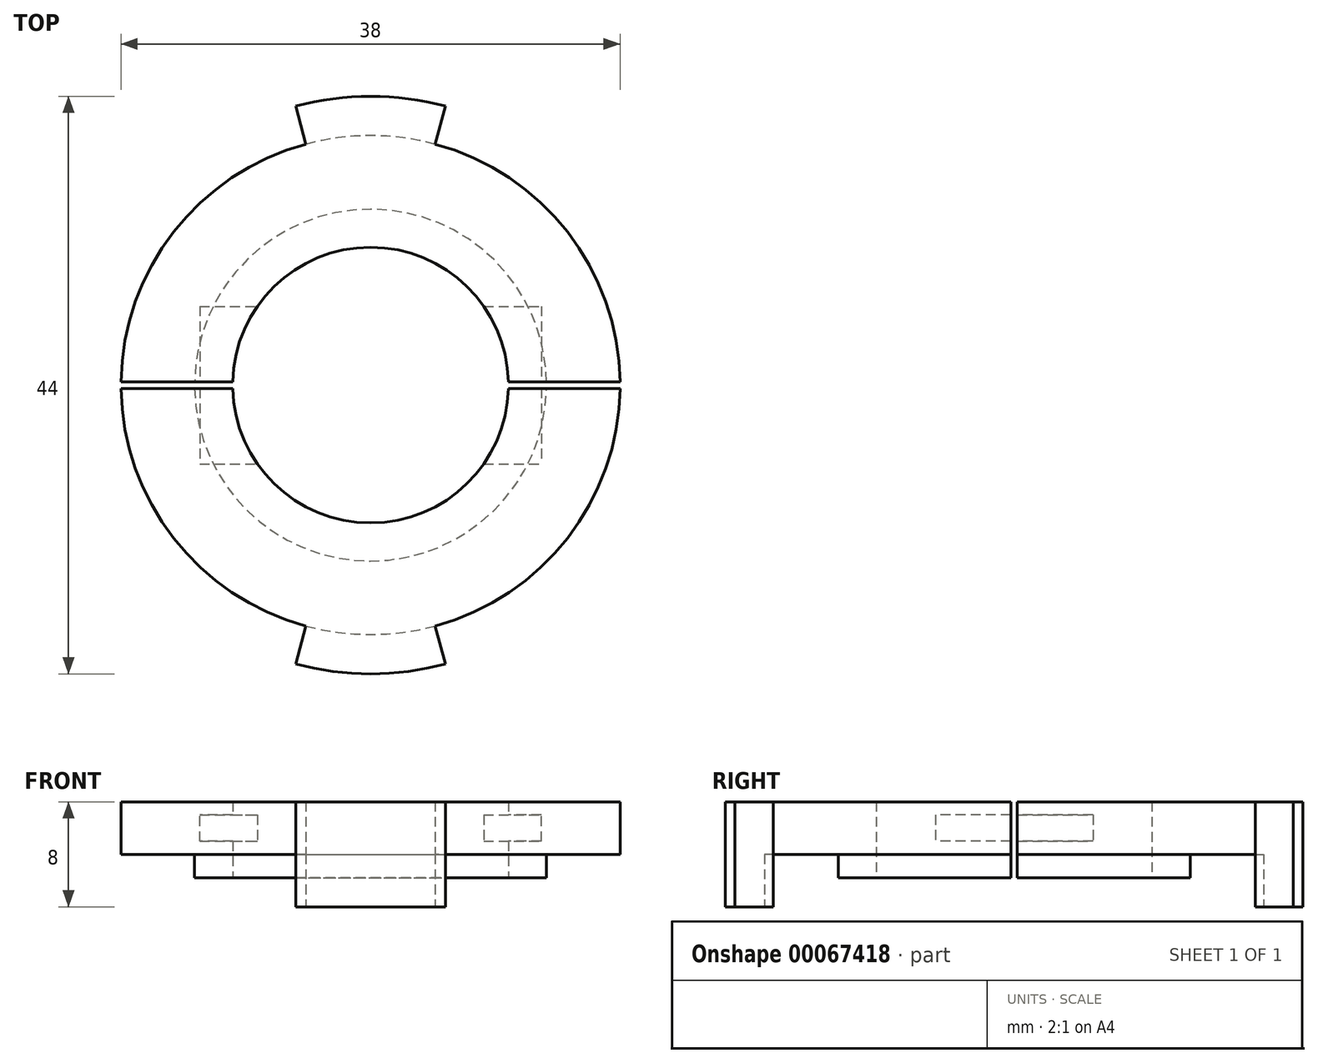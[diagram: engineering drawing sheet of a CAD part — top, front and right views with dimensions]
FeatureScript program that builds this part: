
annotation { "Feature Type Name" : "Feature", "Feature Type Description" : "" }
export const myFeature = defineFeature(function(context is Context, id is Id, definition is map)
    precondition{}
    {
        {
            var Q0;
            Q0=qCreatedBy(makeId("Top.planeOp"),FACE);
            var sketch = newSketch(context, id + "F0", { "sketchPlane" : qUnion([Q0])});
            skCircle(sketch, "E0", {"center": v(0, 0) * mm, "radius": 13.4 * mm});
            skCircle(sketch, "E1", {"center": v(0, 0) * mm, "radius": 19 * mm});
            skCircle(sketch, "E2", {"center": v(0, 0) * mm, "radius": 10.5 * mm});
            skSolve(sketch);
        }
        {
            var Q0;
            Q0=makeQuery(id+"F0.imprint","IMPRINT",FACE,{"disambiguationData":[TD([[makeQuery(id+"F0.imprint","IMPRINT",EDGE,{"derivedFrom":sQuery(id+"F0.wireOp",EDGE,"E0")}),-1.0]])]});
            var Q1;
            Q1=makeQuery(id+"F0.imprint","IMPRINT",FACE,{"disambiguationData":[TD([[makeQuery(id+"F0.imprint","IMPRINT",EDGE,{"derivedFrom":sQuery(id+"F0.wireOp",EDGE,"E0")}),1.0]])]});
            extrude(context, id + "F1", {"entities" : qUnion([Q0, Q1]), "depth" : 4 * mm});
        }
        {
            var Q0;
            Q0=makeQuery(id+"F0.imprint","IMPRINT",FACE,{"disambiguationData":[TD([[makeQuery(id+"F0.imprint","IMPRINT",EDGE,{"derivedFrom":sQuery(id+"F0.wireOp",EDGE,"E0")}),1.0]])]});
            extrude(context, id + "F2", {"entities" : qUnion([Q0]), "operationType" : NewBodyOperationType.ADD, "oppositeDirection" : true, "depth" : 1.8 * mm});
        }
        {
            var Q0;
            Q0=qCreatedBy(makeId("Right.planeOp"),FACE);
            var sketch = newSketch(context, id + "F3", { "sketchPlane" : qUnion([Q0])});
            skLineSegment(sketch, "E3", {"start": v(0, 0) * mm, "end": v(0, 4) * mm});
            skLineSegment(sketch, "E4.rect.bottom", {"start": v(6, 3) * mm, "end": v(-6, 3) * mm});
            skLineSegment(sketch, "E4.rect.top", {"start": v(6, 1) * mm, "end": v(-6, 1) * mm});
            skLineSegment(sketch, "E4.rect.left", {"start": v(6, 3) * mm, "end": v(6, 1) * mm});
            skLineSegment(sketch, "E4.rect.right", {"start": v(-6, 3) * mm, "end": v(-6, 1) * mm});
            skPoint(sketch, "E4.rect.middle", {"position": v(0, 2) * mm});
            skSolve(sketch);
        }
        {
            var Q0;
            Q0 = qSketchRegion(id + "F3", true);
            extrude(context, id + "F4", {"entities" : qUnion([Q0]), "operationType" : NewBodyOperationType.REMOVE, "endBound" : BoundingType.SYMMETRIC, "oppositeDirection" : true, "depth" : 26 * mm});
        }
        {
            var Q0;
            Q0=makeQuery(id+"F1.opExtrude","CAP_FACE",FACE,{"disambiguationData":[OSD([sQuery(id+"F0.wireOp",EDGE,"E1"),sQuery(id+"F0.wireOp",EDGE,"E2")])],"isStart":false});
            var sketch = newSketch(context, id + "F5", { "sketchPlane" : qUnion([Q0])});
            skLineSegment(sketch, "E5.rect.bottom", {"start": v(20, 0.25) * mm, "end": v(-20, 0.25) * mm});
            skLineSegment(sketch, "E5.rect.top", {"start": v(20, -0.25) * mm, "end": v(-20, -0.25) * mm});
            skLineSegment(sketch, "E5.rect.left", {"start": v(20, 0.25) * mm, "end": v(20, -0.25) * mm});
            skLineSegment(sketch, "E5.rect.right", {"start": v(-20, 0.25) * mm, "end": v(-20, -0.25) * mm});
            skPoint(sketch, "E5.rect.middle", {"position": v(0, 0) * mm});
            skSolve(sketch);
        }
        {
            var Q0;
            {var subQ0=sQuery(id+"F5.wireOp",EDGE,"E5.rect.bottom");var subQ1=makeQuery(id+"F1.opExtrude","CAP_EDGE",EDGE,{"disambiguationData":[OSD([sQuery(id+"F0.wireOp",EDGE,"E2")])],"isStart":false});var subQ2=makeQuery(id+"F5.imprint","INTERSECT",VERTEX,{"disambiguationData":[OD(0.0)],"derivedFrom":[subQ1,subQ0]});Q0=makeQuery(id+"F5.imprint","IMPRINT",FACE,{"disambiguationData":[TD([[makeQuery(id+"F5.imprint","IMPRINT",EDGE,{"disambiguationData":[TD([[subQ2,-1.0]])],"derivedFrom":subQ0}),1.0]])]});}
            var Q1;
            Q1 = qSketchRegion(id + "F5", true);
            extrude(context, id + "F6", {"entities" : qUnion([Q0, Q1]), "operationType" : NewBodyOperationType.REMOVE, "oppositeDirection" : true, "depth" : 25 * mm});
        }
        {
            var Q0;
            Q0=qCreatedBy(makeId("Top.planeOp"),FACE);
            var sketch = newSketch(context, id + "F7", { "sketchPlane" : qUnion([Q0])});
            skCircle(sketch, "E6", {"center": v(0, 0) * mm, "radius": 22 * mm});
            skLineSegment(sketch, "E7", {"start": v(0, 0) * mm, "end": v(-7.19, 26.82) * mm});
            skLineSegment(sketch, "E8", {"start": v(0, 0) * mm, "end": v(7.6, 28.39) * mm});
            skLineSegment(sketch, "E9", {"start": v(0, 0) * mm, "end": v(2.47, 0) * mm});
            skLineSegment(sketch, "E10.MirrorCS", {"start": v(0, 0) * mm, "end": v(7.6, -28.39) * mm});
            skLineSegment(sketch, "E11.MirrorCS", {"start": v(0, 0) * mm, "end": v(-7.19, -26.82) * mm});
            skArc(sketch, "E12.0", {"start": v(19, 0.25) * mm, "mid": v(0, 19) * mm, "end": v(-19, 0.25) * mm});
            skArc(sketch, "E13.0", {"start": v(-19, -0.25) * mm, "mid": v(0, -19) * mm, "end": v(19, -0.25) * mm});
            skSolve(sketch);
        }
        {
            var Q0;
            {var subQ0=sQuery(id+"F7.wireOp",EDGE,"E11.MirrorCS");var subQ1=sQuery(id+"F7.wireOp",EDGE,"E6");var subQ2=makeQuery(id+"F7.imprint","INTERSECT",VERTEX,{"derivedFrom":[subQ1,subQ0]});Q0=makeQuery(id+"F7.imprint","IMPRINT",FACE,{"disambiguationData":[TD([[makeQuery(id+"F7.imprint","IMPRINT",EDGE,{"disambiguationData":[TD([[subQ2,-1.0]])],"derivedFrom":subQ1}),1.0]])]});}
            var Q1;
            {var subQ0=sQuery(id+"F7.wireOp",EDGE,"E7");var subQ1=sQuery(id+"F7.wireOp",EDGE,"E6");var subQ2=makeQuery(id+"F7.imprint","INTERSECT",VERTEX,{"derivedFrom":[subQ1,subQ0]});Q1=makeQuery(id+"F7.imprint","IMPRINT",FACE,{"disambiguationData":[TD([[makeQuery(id+"F7.imprint","IMPRINT",EDGE,{"disambiguationData":[TD([[subQ2,1.0]])],"derivedFrom":subQ1}),1.0]])]});}
            extrude(context, id + "F8", {"entities" : qUnion([Q0, Q1]), "operationType" : NewBodyOperationType.ADD, "endBound" : BoundingType.SYMMETRIC, "depth" : 8 * mm});
        }
    });
